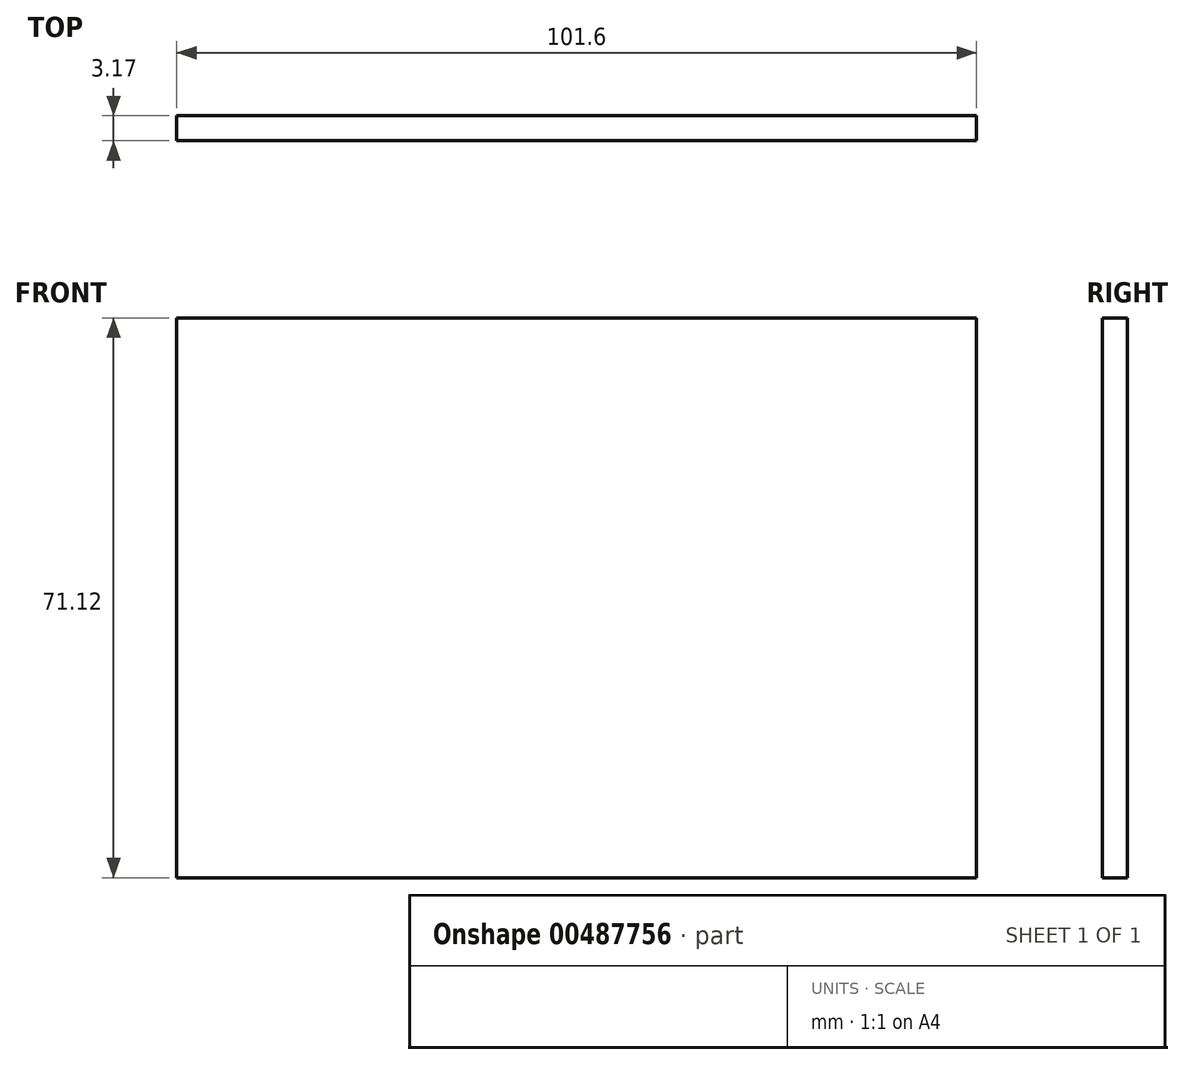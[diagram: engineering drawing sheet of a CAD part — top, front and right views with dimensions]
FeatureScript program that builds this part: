
annotation { "Feature Type Name" : "Feature", "Feature Type Description" : "" }
export const myFeature = defineFeature(function(context is Context, id is Id, definition is map)
    precondition{}
    {
        {
            var Q0;
            Q0=qCreatedBy(makeId("Front.planeOp"),FACE);
            var sketch = newSketch(context, id + "F0", { "sketchPlane" : qUnion([Q0])});
            skLineSegment(sketch, "E0.bottom", {"start": v(-50.8, 35.56) * mm, "end": v(50.8, 35.56) * mm});
            skLineSegment(sketch, "E0.top", {"start": v(-50.8, -35.56) * mm, "end": v(50.8, -35.56) * mm});
            skLineSegment(sketch, "E0.left", {"start": v(-50.8, 35.56) * mm, "end": v(-50.8, -35.56) * mm});
            skLineSegment(sketch, "E0.right", {"start": v(50.8, 35.56) * mm, "end": v(50.8, -35.56) * mm});
            skPoint(sketch, "E0.middle", {"position": v(0, 0) * mm});
            skSolve(sketch);
        }
        {
            var Q0;
            Q0 = qSketchRegion(id + "F0", true);
            extrude(context, id + "F1", {"entities" : qUnion([Q0]), "depth" : 3.17 * mm});
        }
    });
